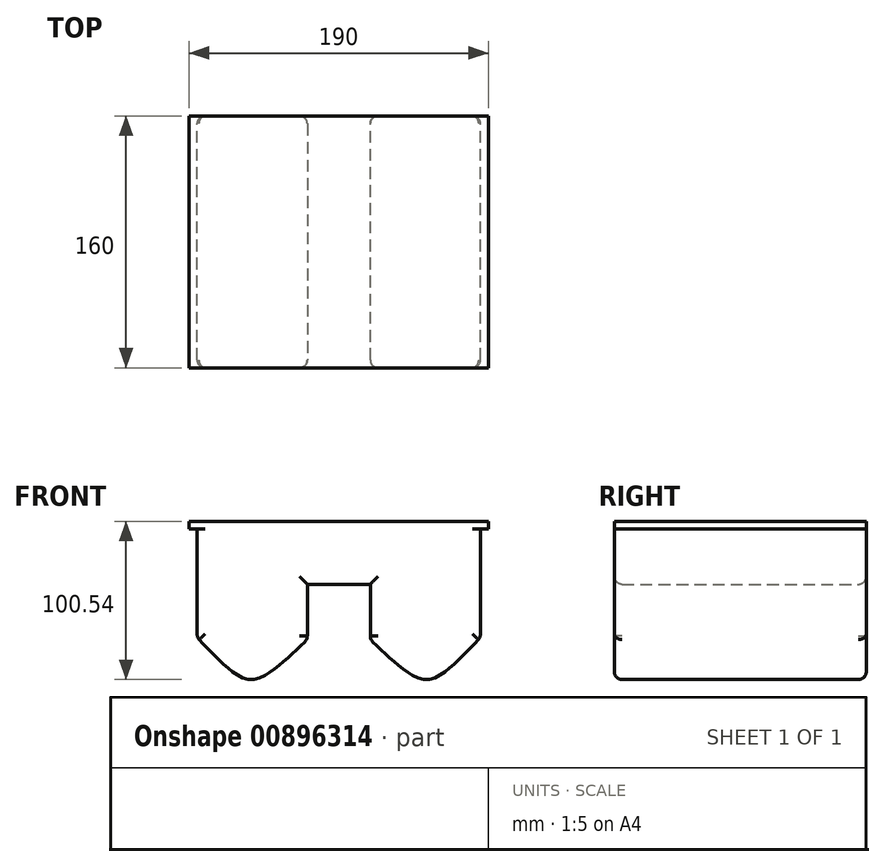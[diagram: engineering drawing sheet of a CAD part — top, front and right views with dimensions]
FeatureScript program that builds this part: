
annotation { "Feature Type Name" : "Feature", "Feature Type Description" : "" }
export const myFeature = defineFeature(function(context is Context, id is Id, definition is map)
    precondition{}
    {
        {
            var Q0;
            Q0=qCreatedBy(makeId("Front.planeOp"),FACE);
            var sketch = newSketch(context, id + "F0", { "sketchPlane" : qUnion([Q0])});
            skLineSegment(sketch, "E0", {"start": v(-15, 49.74) * mm, "end": v(-90, 49.74) * mm});
            skPoint(sketch, "E1", {"position": v(-52.5, 49.74) * mm});
            skLineSegment(sketch, "E2", {"start": v(0, 0) * mm, "end": v(0, 75.41) * mm});
            skLineSegment(sketch, "E3", {"start": v(0, 75.41) * mm, "end": v(0, -74.11) * mm});
            skLineSegment(sketch, "E4.MirrorCS", {"start": v(15, 49.74) * mm, "end": v(90, 49.74) * mm});
            skLineSegment(sketch, "E5", {"start": v(-15, 49.74) * mm, "end": v(15, 49.74) * mm});
            skPoint(sketch, "E6", {"position": v(52.5, 49.74) * mm});
            skLineSegment(sketch, "E7", {"start": v(-90, 49.74) * mm, "end": v(-95, 49.74) * mm});
            skLineSegment(sketch, "E8", {"start": v(-95, 49.74) * mm, "end": v(-95, 44.74) * mm});
            skLineSegment(sketch, "E9", {"start": v(-95, 44.74) * mm, "end": v(-90, 44.74) * mm});
            skLineSegment(sketch, "E10", {"start": v(-90, 44.74) * mm, "end": v(-90, -3.9) * mm});
            skLineSegment(sketch, "E11", {"start": v(-90, -3.9) * mm, "end": v(-90, -23.9) * mm});
            skLineSegment(sketch, "E12", {"start": v(-15, 49.74) * mm, "end": v(-15, 44.74) * mm});
            skLineSegment(sketch, "E13", {"start": v(-15, 44.74) * mm, "end": v(-20, 44.74) * mm});
            skLineSegment(sketch, "E14", {"start": v(-20, 44.74) * mm, "end": v(-20, -25.26) * mm});
            skFitSpline(sketch, "E15", {"points": [v(-90, -23.9) * mm, v(-20, -25.26) * mm], "startDerivative": vector(101.86, -106.86) * mm, "endDerivative": vector(108.14, 102.8) * mm});
            skLineSegment(sketch, "E16.MirrorCS", {"start": v(20, 44.74) * mm, "end": v(20, -25.26) * mm});
            skLineSegment(sketch, "E17.MirrorCS", {"start": v(15, 44.74) * mm, "end": v(20, 44.74) * mm});
            skLineSegment(sketch, "E18.MirrorCS", {"start": v(15, 49.74) * mm, "end": v(15, 44.74) * mm});
            skFitSpline(sketch, "E19.MirrorCS", {"points": [v(90, -23.9) * mm, v(20, -25.26) * mm], "startDerivative": vector(-101.86, -106.86) * mm, "endDerivative": vector(-108.14, 102.8) * mm});
            skLineSegment(sketch, "E20.MirrorCS", {"start": v(90, -3.9) * mm, "end": v(90, -23.9) * mm});
            skLineSegment(sketch, "E21.MirrorCS", {"start": v(90, 44.74) * mm, "end": v(90, -3.9) * mm});
            skLineSegment(sketch, "E22.MirrorCS", {"start": v(95, 44.74) * mm, "end": v(90, 44.74) * mm});
            skLineSegment(sketch, "E23.MirrorCS", {"start": v(95, 49.74) * mm, "end": v(95, 44.74) * mm});
            skLineSegment(sketch, "E24.MirrorCS", {"start": v(90, 49.74) * mm, "end": v(95, 49.74) * mm});
            skLineSegment(sketch, "E25", {"start": v(-20, 9.74) * mm, "end": v(20, 9.74) * mm});
            skLineSegment(sketch, "E26.bottom", {"start": v(497.95, -126.75) * mm, "end": v(773.3, -126.75) * mm});
            skLineSegment(sketch, "E26.top", {"start": v(497.95, -48.82) * mm, "end": v(773.3, -48.82) * mm});
            skArc(sketch, "E27", {"start": v(497.95, -48.82) * mm, "mid": v(465.24, -87.78) * mm, "end": v(497.95, -126.75) * mm});
            skLineSegment(sketch, "E28", {"start": v(821.1, -83.74) * mm, "end": v(773.3, -48.82) * mm});
            skLineSegment(sketch, "E29.MirrorCS", {"start": v(821.1, -91.82) * mm, "end": v(773.3, -126.75) * mm});
            skPoint(sketch, "E30.visualSharp", {"position": v(826.62, -87.78) * mm});
            skArc(sketch, "E30.filletArc", {"start": v(821.1, -91.82) * mm, "mid": v(823.14, -87.78) * mm, "end": v(821.1, -83.74) * mm});
            skArc(sketch, "E31.0", {"start": v(824.04, -95.85) * mm, "mid": v(828.14, -87.78) * mm, "end": v(824.04, -79.7) * mm});
            skLineSegment(sketch, "E31.1", {"start": v(497.53, -43.82) * mm, "end": v(774.94, -43.82) * mm});
            skArc(sketch, "E31.2", {"start": v(497.53, -43.82) * mm, "mid": v(460.24, -87.78) * mm, "end": v(497.53, -131.75) * mm});
            skLineSegment(sketch, "E31.3", {"start": v(824.04, -79.7) * mm, "end": v(774.94, -43.82) * mm});
            skLineSegment(sketch, "E31.4", {"start": v(497.53, -131.75) * mm, "end": v(774.94, -131.75) * mm});
            skLineSegment(sketch, "E31.5", {"start": v(824.04, -95.85) * mm, "end": v(774.94, -131.75) * mm});
            skArc(sketch, "E32.0", {"start": v(497.13, -38.82) * mm, "mid": v(455.24, -87.78) * mm, "end": v(497.13, -136.75) * mm});
            skLineSegment(sketch, "E32.1", {"start": v(827, -75.67) * mm, "end": v(776.57, -38.82) * mm});
            skArc(sketch, "E32.2", {"start": v(827, -99.9) * mm, "mid": v(833.14, -87.78) * mm, "end": v(827, -75.67) * mm});
            skLineSegment(sketch, "E32.3", {"start": v(497.13, -38.82) * mm, "end": v(776.57, -38.82) * mm});
            skLineSegment(sketch, "E32.4", {"start": v(827, -99.9) * mm, "end": v(776.57, -136.75) * mm});
            skLineSegment(sketch, "E32.5", {"start": v(497.13, -136.75) * mm, "end": v(776.57, -136.75) * mm});
            skSolve(sketch);
        }
        {
            var Q0;
            Q0=makeQuery(id+"F0.imprint","IMPRINT",FACE,{"disambiguationData":[TD([[makeQuery(id+"F0.imprint","IMPRINT",EDGE,{"derivedFrom":sQuery(id+"F0.wireOp",EDGE,"E0")}),1.0]])]});
            var Q1;
            Q1=makeQuery(id+"F0.imprint","IMPRINT",FACE,{"disambiguationData":[TD([[makeQuery(id+"F0.imprint","IMPRINT",EDGE,{"derivedFrom":sQuery(id+"F0.wireOp",EDGE,"E4.MirrorCS")}),-1.0]])]});
            var Q2;
            {var subQ0=sQuery(id+"F0.wireOp",EDGE,"E12");Q2=makeQuery(id+"F0.imprint","IMPRINT",FACE,{"disambiguationData":[TD([[makeQuery(id+"F0.imprint","IMPRINT",EDGE,{"derivedFrom":subQ0}),1.0]])]});}
            var Q3;
            {var subQ0=sQuery(id+"F0.wireOp",EDGE,"E17.MirrorCS");Q3=makeQuery(id+"F0.imprint","IMPRINT",FACE,{"disambiguationData":[TD([[makeQuery(id+"F0.imprint","IMPRINT",EDGE,{"derivedFrom":subQ0}),-1.0]])]});}
            extrude(context, id + "F1", {"entities" : qUnion([Q0, Q1, Q2, Q3]), "depth" : 160 * mm, "offsetDistance" : 25 * mm});
        }
        {
            var Q0;
            Q0=makeQuery(id+"F1.opExtrude","CAP_EDGE",EDGE,{"disambiguationData":[OSD([sQuery(id+"F0.wireOp",EDGE,"E25")])],"isStart":false});
            var Q1;
            Q1=makeQuery(id+"F1.opExtrude","CAP_EDGE",EDGE,{"disambiguationData":[OSD([sQuery(id+"F0.wireOp",EDGE,"E16.MirrorCS")])],"isStart":false});
            var Q2;
            Q2=makeQuery(id+"F1.opExtrude","CAP_EDGE",EDGE,{"disambiguationData":[OSD([sQuery(id+"F0.wireOp",EDGE,"E14")])],"isStart":false});
            var Q3;
            Q3=makeQuery(id+"F1.opExtrude","CAP_EDGE",EDGE,{"disambiguationData":[OSD([sQuery(id+"F0.wireOp",EDGE,"E14")])],"isStart":true});
            var Q4;
            Q4=makeQuery(id+"F1.opExtrude","CAP_EDGE",EDGE,{"disambiguationData":[OSD([sQuery(id+"F0.wireOp",EDGE,"E25")])],"isStart":true});
            var Q5;
            Q5=makeQuery(id+"F1.opExtrude","CAP_EDGE",EDGE,{"disambiguationData":[OSD([sQuery(id+"F0.wireOp",EDGE,"E16.MirrorCS")])],"isStart":true});
            fillet(context, id + "F2", {"entities" : qUnion([Q0, Q1, Q2, Q3, Q4, Q5]), "radius" : 5 * mm, "tangentPropagation" : true, "allowEdgeOverflow" : false});
        }
        {
            var Q0;
            Q0=makeQuery(id+"F1.opExtrude","CAP_EDGE",EDGE,{"disambiguationData":[OSD([sQuery(id+"F0.wireOp",EDGE,"E19.MirrorCS")])],"isStart":false});
            var Q1;
            Q1=makeQuery(id+"F1.opExtrude","CAP_EDGE",EDGE,{"disambiguationData":[OSD([sQuery(id+"F0.wireOp",EDGE,"E15")])],"isStart":false});
            var Q2;
            Q2=makeQuery(id+"F1.opExtrude","CAP_EDGE",EDGE,{"disambiguationData":[OSD([sQuery(id+"F0.wireOp",EDGE,"E15")])],"isStart":true});
            var Q3;
            Q3=makeQuery(id+"F1.opExtrude","CAP_EDGE",EDGE,{"disambiguationData":[OSD([sQuery(id+"F0.wireOp",EDGE,"E19.MirrorCS")])],"isStart":true});
            fillet(context, id + "F3", {"entities" : qUnion([Q0, Q1, Q2, Q3]), "radius" : 5 * mm, "tangentPropagation" : true, "allowEdgeOverflow" : false});
        }
        {
            var Q0;
            Q0=makeQuery(id+"F1.opExtrude","SWEPT_EDGE",EDGE,{"disambiguationData":[OSD([sQuery(id+"F0.wireOp",EDGE,"E19.MirrorCS"),sQuery(id+"F0.wireOp",EDGE,"E20.MirrorCS")])]});
            var Q1;
            Q1=makeQuery(id+"F1.opExtrude","SWEPT_EDGE",EDGE,{"disambiguationData":[OSD([sQuery(id+"F0.wireOp",EDGE,"E11"),sQuery(id+"F0.wireOp",EDGE,"E15")])]});
            fillet(context, id + "F4", {"entities" : qUnion([Q0, Q1]), "radius" : 5 * mm, "tangentPropagation" : true, "allowEdgeOverflow" : false});
        }
    });
